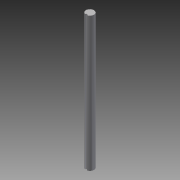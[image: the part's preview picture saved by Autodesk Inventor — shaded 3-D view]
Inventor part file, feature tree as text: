
AUTODESK INVENTOR PART (.ipt)
format: ipt  version: 2013 (Build 170138000, 138)  size: 75,776 bytes
history: native  units: in
note: dims shown in document units (in); Inventor stores cm internally (conversion verified against a paired STEP export)
features: extrude x1, sketch x1
ambient origin geometry x8: Origin, YZ Plane, XZ Plane, XY Plane, X Axis, Y Axis, Z Axis, Center Point
bodies: Solid1 (feature_tree)
feature tree (2):
  extrude  "Extrusion1"  Depth=0.0787in
  sketch  "Sketch1"  dims[d0=0.315in d1=0.0787in d2=0.0394in d3=0.0394in d4=5.25in d5=0.0in]
